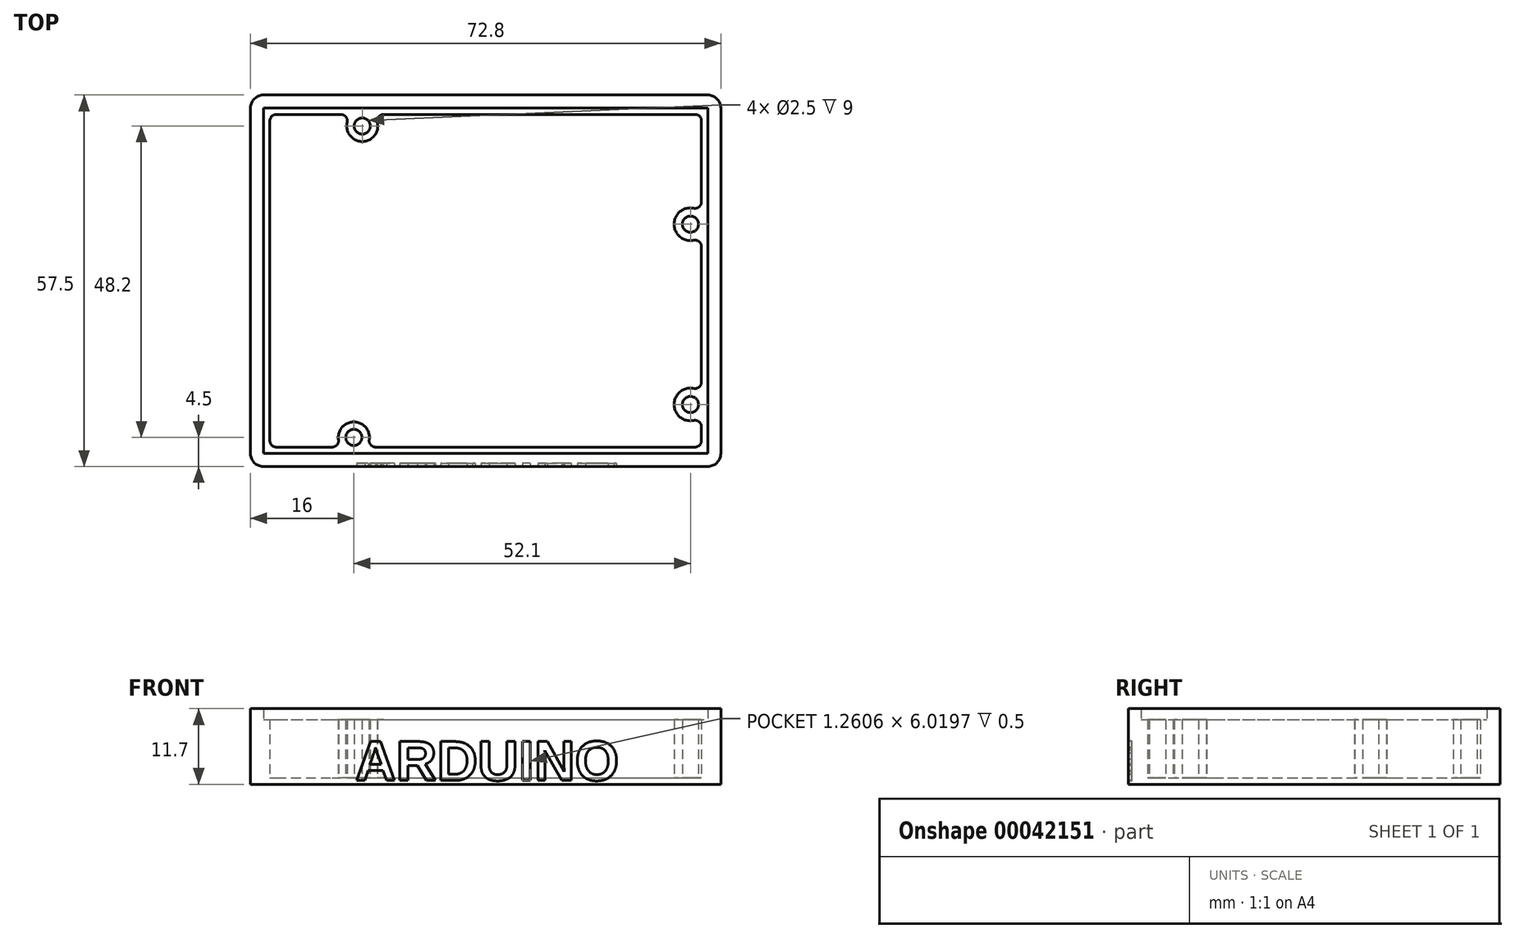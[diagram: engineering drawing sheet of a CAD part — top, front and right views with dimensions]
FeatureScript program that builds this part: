
annotation { "Feature Type Name" : "Feature", "Feature Type Description" : "" }
export const myFeature = defineFeature(function(context is Context, id is Id, definition is map)
    precondition{}
    {
        {
            var Q0;
            Q0=qCreatedBy(makeId("Top.planeOp"),FACE);
            var sketch = newSketch(context, id + "F0", { "sketchPlane" : qUnion([Q0])});
            skLineSegment(sketch, "E0.bottom", {"start": v(0, 0) * mm, "end": v(68.8, 0) * mm});
            skLineSegment(sketch, "E0.top", {"start": v(0, 53.5) * mm, "end": v(68.8, 53.5) * mm});
            skLineSegment(sketch, "E0.left", {"start": v(0, 0) * mm, "end": v(0, 53.5) * mm});
            skLineSegment(sketch, "E0.right", {"start": v(68.8, 0) * mm, "end": v(68.8, 53.5) * mm});
            skPoint(sketch, "E1.center.orphan", {"position": v(14, 2.5) * mm});
            skPoint(sketch, "E2.start.orphan", {"position": v(15.3, 0) * mm});
            skPoint(sketch, "E3.start.orphan", {"position": v(14, 0) * mm});
            skPoint(sketch, "E4.start.orphan", {"position": v(66.1, 0) * mm});
            skPoint(sketch, "E5.trimOffspring.end.orphan", {"position": v(15.3, 53.5) * mm});
            skPoint(sketch, "E6.trimOffspring.end.orphan", {"position": v(14, 53.5) * mm});
            skPoint(sketch, "E7.visualSharp", {"position": v(67.8, 37.37) * mm});
            skPoint(sketch, "E8.visualSharp", {"position": v(67.8, 33.63) * mm});
            skPoint(sketch, "E9.visualSharp", {"position": v(67.8, 9.47) * mm});
            skPoint(sketch, "E10.visualSharp", {"position": v(67.8, 5.73) * mm});
            skPoint(sketch, "E11.visualSharp", {"position": v(12.13, 1) * mm});
            skPoint(sketch, "E12.visualSharp", {"position": v(15.87, 1) * mm});
            skLineSegment(sketch, "E13.0", {"start": v(-2, 0) * mm, "end": v(-2, 53.5) * mm});
            skLineSegment(sketch, "E13.1", {"start": v(0, -2) * mm, "end": v(68.8, -2) * mm});
            skLineSegment(sketch, "E13.2", {"start": v(70.8, 0) * mm, "end": v(70.8, 53.5) * mm});
            skLineSegment(sketch, "E13.3", {"start": v(0, 55.5) * mm, "end": v(68.8, 55.5) * mm});
            skPoint(sketch, "E14.trimOffspring.end.orphan", {"position": v(66.1, 53.5) * mm});
            skPoint(sketch, "E15", {"position": v(15.3, 50.7) * mm});
            skPoint(sketch, "E16", {"position": v(66.1, 35.5) * mm});
            skPoint(sketch, "E17", {"position": v(66.1, 7.6) * mm});
            skArc(sketch, "E18", {"start": v(12.97, 51.26) * mm, "mid": v(15.3, 48.3) * mm, "end": v(17.63, 51.26) * mm});
            skArc(sketch, "E19", {"start": v(66.6, 37.98) * mm, "mid": v(63.57, 35.5) * mm, "end": v(66.6, 33.02) * mm});
            skArc(sketch, "E20", {"start": v(66.6, 10.08) * mm, "mid": v(63.57, 7.6) * mm, "end": v(66.6, 5.12) * mm});
            skArc(sketch, "E21", {"start": v(16.37, 2.15) * mm, "mid": v(14, 4.9) * mm, "end": v(11.63, 2.15) * mm});
            skLineSegment(sketch, "E22.0", {"start": v(2, 52.5) * mm, "end": v(12, 52.5) * mm});
            skLineSegment(sketch, "E22.1", {"start": v(1, 2) * mm, "end": v(1, 51.5) * mm});
            skLineSegment(sketch, "E22.2", {"start": v(2, 1) * mm, "end": v(10.64, 1) * mm});
            skLineSegment(sketch, "E22.3", {"start": v(67.8, 2) * mm, "end": v(67.8, 4.14) * mm});
            skLineSegment(sketch, "E23.trimOffspring", {"start": v(18.6, 52.5) * mm, "end": v(66.8, 52.5) * mm});
            skPoint(sketch, "E24.visualSharp", {"position": v(13.71, 52.5) * mm});
            skArc(sketch, "E24.filletArc", {"start": v(12.97, 51.26) * mm, "mid": v(12.78, 52.12) * mm, "end": v(12, 52.5) * mm});
            skPoint(sketch, "E25.visualSharp", {"position": v(16.89, 52.5) * mm});
            skArc(sketch, "E25.filletArc", {"start": v(18.6, 52.5) * mm, "mid": v(17.82, 52.12) * mm, "end": v(17.63, 51.26) * mm});
            skLineSegment(sketch, "E26.trimOffspring", {"start": v(17.36, 1) * mm, "end": v(66.8, 1) * mm});
            skArc(sketch, "E27.filletArc", {"start": v(10.64, 1) * mm, "mid": v(11.4, 1.35) * mm, "end": v(11.63, 2.15) * mm});
            skArc(sketch, "E28.filletArc", {"start": v(16.37, 2.15) * mm, "mid": v(16.6, 1.35) * mm, "end": v(17.36, 1) * mm});
            skLineSegment(sketch, "E29.trimOffspring", {"start": v(67.8, 11.06) * mm, "end": v(67.8, 32.04) * mm});
            skArc(sketch, "E30.filletArc", {"start": v(66.6, 10.08) * mm, "mid": v(67.43, 10.29) * mm, "end": v(67.8, 11.06) * mm});
            skArc(sketch, "E31.filletArc", {"start": v(67.8, 4.14) * mm, "mid": v(67.43, 4.91) * mm, "end": v(66.6, 5.12) * mm});
            skLineSegment(sketch, "E32.trimOffspring", {"start": v(67.8, 38.96) * mm, "end": v(67.8, 51.5) * mm});
            skArc(sketch, "E33.filletArc", {"start": v(66.6, 37.98) * mm, "mid": v(67.43, 38.19) * mm, "end": v(67.8, 38.96) * mm});
            skArc(sketch, "E34.filletArc", {"start": v(67.8, 32.04) * mm, "mid": v(67.43, 32.81) * mm, "end": v(66.6, 33.02) * mm});
            skPoint(sketch, "E35.visualSharp", {"position": v(1, 52.5) * mm});
            skArc(sketch, "E35.filletArc", {"start": v(2, 52.5) * mm, "mid": v(1.3, 52.2) * mm, "end": v(1, 51.5) * mm});
            skPoint(sketch, "E36.visualSharp", {"position": v(67.8, 52.5) * mm});
            skArc(sketch, "E36.filletArc", {"start": v(67.8, 51.5) * mm, "mid": v(67.5, 52.2) * mm, "end": v(66.8, 52.5) * mm});
            skPoint(sketch, "E37.visualSharp", {"position": v(1, 1) * mm});
            skArc(sketch, "E37.filletArc", {"start": v(1, 2) * mm, "mid": v(1.3, 1.3) * mm, "end": v(2, 1) * mm});
            skPoint(sketch, "E38.visualSharp", {"position": v(67.8, 1) * mm});
            skArc(sketch, "E38.filletArc", {"start": v(66.8, 1) * mm, "mid": v(67.5, 1.3) * mm, "end": v(67.8, 2) * mm});
            skPoint(sketch, "E39.visualSharp", {"position": v(-2, 55.5) * mm});
            skArc(sketch, "E39.filletArc", {"start": v(0, 55.5) * mm, "mid": v(-1.41, 54.91) * mm, "end": v(-2, 53.5) * mm});
            skPoint(sketch, "E40.visualSharp", {"position": v(70.8, 55.5) * mm});
            skArc(sketch, "E40.filletArc", {"start": v(70.8, 53.5) * mm, "mid": v(70.21, 54.91) * mm, "end": v(68.8, 55.5) * mm});
            skPoint(sketch, "E41.visualSharp", {"position": v(70.8, -2) * mm});
            skArc(sketch, "E41.filletArc", {"start": v(68.8, -2) * mm, "mid": v(70.21, -1.41) * mm, "end": v(70.8, 0) * mm});
            skPoint(sketch, "E42.visualSharp", {"position": v(-2, -2) * mm});
            skArc(sketch, "E42.filletArc", {"start": v(-2, 0) * mm, "mid": v(-1.41, -1.41) * mm, "end": v(0, -2) * mm});
            skCircle(sketch, "E43", {"center": v(15.3, 50.7) * mm, "radius": 1.25 * mm});
            skCircle(sketch, "E44", {"center": v(14, 2.5) * mm, "radius": 1.25 * mm});
            skCircle(sketch, "E45", {"center": v(66.1, 7.6) * mm, "radius": 1.25 * mm});
            skCircle(sketch, "E46", {"center": v(66.1, 35.5) * mm, "radius": 1.25 * mm});
            skSolve(sketch);
        }
        {
            var Q0;
            Q0 = qSketchRegion(id + "F0", true);
            extrude(context, id + "F1", {"entities" : qUnion([Q0]), "depth" : 10.7 * mm});
        }
        {
            var Q0;
            Q0=makeQuery(id+"F0.imprint","IMPRINT",FACE,{"disambiguationData":[TD([[makeQuery(id+"F0.imprint","IMPRINT",EDGE,{"derivedFrom":sQuery(id+"F0.wireOp",EDGE,"E0.bottom")}),1.0]])]});
            extrude(context, id + "F2", {"entities" : qUnion([Q0]), "operationType" : NewBodyOperationType.ADD, "depth" : 9 * mm});
        }
        {
            var Q0;
            Q0=makeQuery(id+"F0.imprint","IMPRINT",FACE,{"disambiguationData":[TD([[makeQuery(id+"F0.imprint","IMPRINT",EDGE,{"derivedFrom":sQuery(id+"F0.wireOp",EDGE,"E0.bottom")}),-1.0]])]});
            var Q1;
            Q1=makeQuery(id+"F0.imprint","IMPRINT",FACE,{"disambiguationData":[TD([[makeQuery(id+"F0.imprint","IMPRINT",EDGE,{"derivedFrom":sQuery(id+"F0.wireOp",EDGE,"E0.bottom")}),1.0]])]});
            var Q2;
            Q2=makeQuery(id+"F0.imprint","IMPRINT",FACE,{"disambiguationData":[TD([[makeQuery(id+"F0.imprint","IMPRINT",EDGE,{"derivedFrom":sQuery(id+"F0.wireOp",EDGE,"E18")}),-1.0]])]});
            var Q3;
            Q3=makeQuery(id+"F0.imprint","IMPRINT",FACE,{"disambiguationData":[TD([[makeQuery(id+"F0.imprint","IMPRINT",EDGE,{"derivedFrom":sQuery(id+"F0.wireOp",EDGE,"E44")}),1.0]])]});
            var Q4;
            Q4=makeQuery(id+"F0.imprint","IMPRINT",FACE,{"disambiguationData":[TD([[makeQuery(id+"F0.imprint","IMPRINT",EDGE,{"derivedFrom":sQuery(id+"F0.wireOp",EDGE,"E45")}),1.0]])]});
            var Q5;
            Q5=makeQuery(id+"F0.imprint","IMPRINT",FACE,{"disambiguationData":[TD([[makeQuery(id+"F0.imprint","IMPRINT",EDGE,{"derivedFrom":sQuery(id+"F0.wireOp",EDGE,"E43")}),1.0]])]});
            var Q6;
            Q6=makeQuery(id+"F0.imprint","IMPRINT",FACE,{"disambiguationData":[TD([[makeQuery(id+"F0.imprint","IMPRINT",EDGE,{"derivedFrom":sQuery(id+"F0.wireOp",EDGE,"E46")}),1.0]])]});
            extrude(context, id + "F3", {"entities" : qUnion([Q0, Q1, Q2, Q3, Q4, Q5, Q6]), "operationType" : NewBodyOperationType.ADD, "oppositeDirection" : true, "depth" : 1 * mm});
        }
        {
            var Q0;
            {var subQ0=sQuery(id+"F0.wireOp",EDGE,"E13.1");Q0=makeQuery(id+"F3.boolean.opBoolean","MERGE",FACE,{"derivedFrom":[makeQuery(id+"F1.opExtrude","SWEPT_FACE",FACE,{"disambiguationData":[OSD([subQ0])]}),makeQuery(id+"F3.opExtrude","SWEPT_FACE",FACE,{"disambiguationData":[OSD([subQ0])]})]});}
            var sketch = newSketch(context, id + "F4", { "sketchPlane" : qUnion([Q0])});
            skPoint(sketch, "E47", {"position": v(34.4, 10.7) * mm});
            skPoint(sketch, "E48", {"position": v(34.4, 4.85) * mm});
            skPoint(sketch, "E49.end.orphan", {"position": v(34.4, -1) * mm});
            skText(sketch, "E50", { "text": "ARDUINO", "fontName": "Arimo-Bold.ttf"});
            const initialGuessF4  = {"E50": [0.0142, -0.0004, 1, 0, 0.0063]};
            skSetInitialGuess(sketch, initialGuessF4);
            skSolve(sketch);
        }
        {
            var Q0;
            Q0 = qSketchRegion(id + "F4", true);
            extrude(context, id + "F5", {"entities" : qUnion([Q0]), "operationType" : NewBodyOperationType.REMOVE, "oppositeDirection" : true, "depth" : 0.5 * mm});
        }
    });
